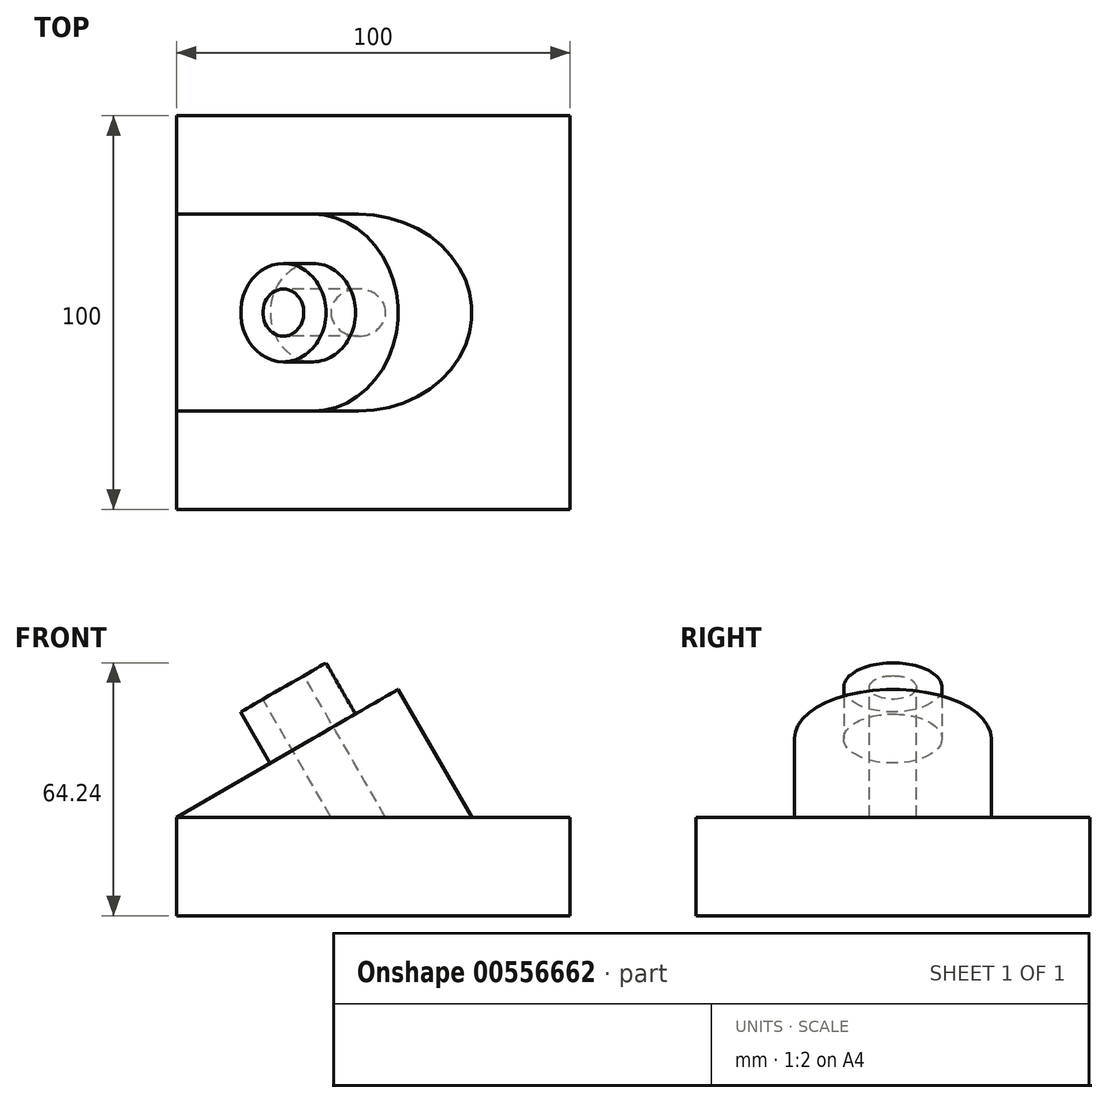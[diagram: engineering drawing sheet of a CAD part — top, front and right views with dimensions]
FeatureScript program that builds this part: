
annotation { "Feature Type Name" : "Feature", "Feature Type Description" : "" }
export const myFeature = defineFeature(function(context is Context, id is Id, definition is map)
    precondition{}
    {
        {
            var Q0;
            Q0=qCreatedBy(makeId("Top.planeOp"),FACE);
            var sketch = newSketch(context, id + "F0", { "sketchPlane" : qUnion([Q0])});
            skLineSegment(sketch, "E0.bottom", {"start": v(0, 0) * mm, "end": v(100, 0) * mm});
            skLineSegment(sketch, "E0.top", {"start": v(0, 100) * mm, "end": v(100, 100) * mm});
            skLineSegment(sketch, "E0.left", {"start": v(0, 0) * mm, "end": v(0, 100) * mm});
            skLineSegment(sketch, "E0.right", {"start": v(100, 0) * mm, "end": v(100, 100) * mm});
            skSolve(sketch);
        }
        {
            var Q0;
            Q0 = qSketchRegion(id + "F0", true);
            extrude(context, id + "F1", {"entities" : qUnion([Q0]), "depth" : 25 * mm, "offsetDistance" : 25 * mm});
        }
        {
            var Q0;
            Q0=makeQuery(id+"F1.opExtrude","CAP_EDGE",EDGE,{"disambiguationData":[OSD([sQuery(id+"F0.wireOp",EDGE,"E0.left")])],"isStart":false});
            cPlane(context, id + "F2", {"entities" : qUnion([Q0]), "cplaneType" : CPlaneType.LINE_ANGLE, "offset" : 25 * mm, "angle" : 30 * degree, "oppositeDirection" : true, "width" : 150 * mm, "height" : 150 * mm});
        }
        {
            var Q0;
            Q0=qCreatedBy(id+"F2.planeOp",FACE);
            var sketch = newSketch(context, id + "F3", { "sketchPlane" : qUnion([Q0])});
            skLineSegment(sketch, "E1.bottom", {"start": v(12.5, 75) * mm, "end": v(77.5, 75) * mm});
            skLineSegment(sketch, "E1.top", {"start": v(12.5, 25) * mm, "end": v(77.5, 25) * mm});
            skLineSegment(sketch, "E1.left", {"start": v(12.5, 75) * mm, "end": v(12.5, 25) * mm});
            skLineSegment(sketch, "E1.right", {"start": v(77.5, 75) * mm, "end": v(77.5, 25) * mm});
            skSolve(sketch);
        }
        {
            var Q0;
            Q0 = qSketchRegion(id + "F3", true);
            extrude(context, id + "F4", {"entities" : qUnion([Q0]), "operationType" : NewBodyOperationType.ADD, "endBound" : BoundingType.UP_TO_NEXT, "oppositeDirection" : true, "depth" : 25 * mm, "offsetDistance" : 25 * mm});
        }
        {
            var Q0;
            Q0=makeQuery(id+"F4.opExtrude","SWEPT_EDGE",EDGE,{"disambiguationData":[OSD([sQuery(id+"F3.wireOp",EDGE,"E1.top"),sQuery(id+"F3.wireOp",EDGE,"E1.right")])]});
            var Q1;
            Q1=makeQuery(id+"F4.opExtrude","SWEPT_EDGE",EDGE,{"disambiguationData":[OSD([sQuery(id+"F3.wireOp",EDGE,"E1.bottom"),sQuery(id+"F3.wireOp",EDGE,"E1.right")])]});
            fillet(context, id + "F5", {"entities" : qUnion([Q0, Q1]), "radius" : 25 * mm, "tangentPropagation" : true, "allowEdgeOverflow" : false});
        }
        {
            var Q0;
            Q0=makeQuery(id+"F4.opExtrude","CAP_FACE",FACE,{"disambiguationData":[OSD([sQuery(id+"F3.wireOp",EDGE,"E1.bottom"),sQuery(id+"F3.wireOp",EDGE,"E1.top"),sQuery(id+"F3.wireOp",EDGE,"E1.left"),sQuery(id+"F3.wireOp",EDGE,"E1.right")])],"isStart":true});
            var sketch = newSketch(context, id + "F6", { "sketchPlane" : qUnion([Q0])});
            skCircle(sketch, "E2", {"center": v(52.5, 50) * mm, "radius": 12.5 * mm});
            skSolve(sketch);
        }
        {
            var Q0;
            Q0 = qSketchRegion(id + "F6", true);
            extrude(context, id + "F7", {"entities" : qUnion([Q0]), "operationType" : NewBodyOperationType.ADD, "depth" : 15 * mm, "offsetDistance" : 25 * mm});
        }
        {
            var Q0;
            Q0=makeQuery(id+"F7.opExtrude","CAP_FACE",FACE,{"disambiguationData":[OSD([sQuery(id+"F6.wireOp",EDGE,"E2")])],"isStart":false});
            var sketch = newSketch(context, id + "F8", { "sketchPlane" : qUnion([Q0])});
            skCircle(sketch, "E3", {"center": v(52.5, 50) * mm, "radius": 6 * mm});
            skSolve(sketch);
        }
        {
            var Q0;
            Q0 = qSketchRegion(id + "F8", true);
            var Q1;
            Q1=makeQuery(id+"F1.opExtrude","CAP_FACE",FACE,{"disambiguationData":[OSD([sQuery(id+"F0.wireOp",EDGE,"E0.bottom"),sQuery(id+"F0.wireOp",EDGE,"E0.top"),sQuery(id+"F0.wireOp",EDGE,"E0.left"),sQuery(id+"F0.wireOp",EDGE,"E0.right")])],"isStart":false});
            var Q2;
            Q2=makeQuery(id+"F1.opExtrude","SWEPT_BODY",BODY,{"disambiguationData":[OSD([sQuery(id+"F0.wireOp",EDGE,"E0.bottom"),sQuery(id+"F0.wireOp",EDGE,"E0.top"),sQuery(id+"F0.wireOp",EDGE,"E0.left"),sQuery(id+"F0.wireOp",EDGE,"E0.right")])]});
            extrude(context, id + "F9", {"entities" : qUnion([Q0]), "operationType" : NewBodyOperationType.REMOVE, "endBound" : BoundingType.UP_TO_SURFACE, "oppositeDirection" : true, "depth" : 25 * mm, "endBoundEntityFace" : qUnion([Q1]), "endBoundEntityBody" : qUnion([Q2]), "offsetDistance" : 25 * mm});
        }
    });
